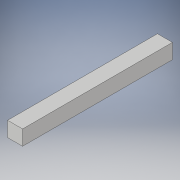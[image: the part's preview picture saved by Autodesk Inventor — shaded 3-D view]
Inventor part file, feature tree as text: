
AUTODESK INVENTOR PART (.ipt)
format: ipt  version: 2019 (Build 230136000, 136)  size: 104,448 bytes
history: native  units: mm
features: delete_face x5, extrude x2, sketch x2
ambient origin geometry x8: Origin, YZ Plane, XZ Plane, XY Plane, X Axis, Y Axis, Z Axis, Center Point
bodies: Solid1 (feature_tree)
feature tree (9):
  extrude  "Extrusion1"  Depth=10.0mm TaperAngle=0.0deg
  delete_face  "Delete Face1"
  delete_face  "Delete Face2"
  delete_face  "Delete Face3"
  delete_face  "Delete Face4"
  delete_face  "Delete Face5"
  extrude  "Extrusion2"  Depth=20.0mm
  sketch  "Sketch1"  dims[d0=100.0mm d1=10.0mm d2=0.0mm]
  sketch  "Sketch2"  dims[d3=200.0mm d4=20.0mm d5=20.0mm d6=0.0mm]
